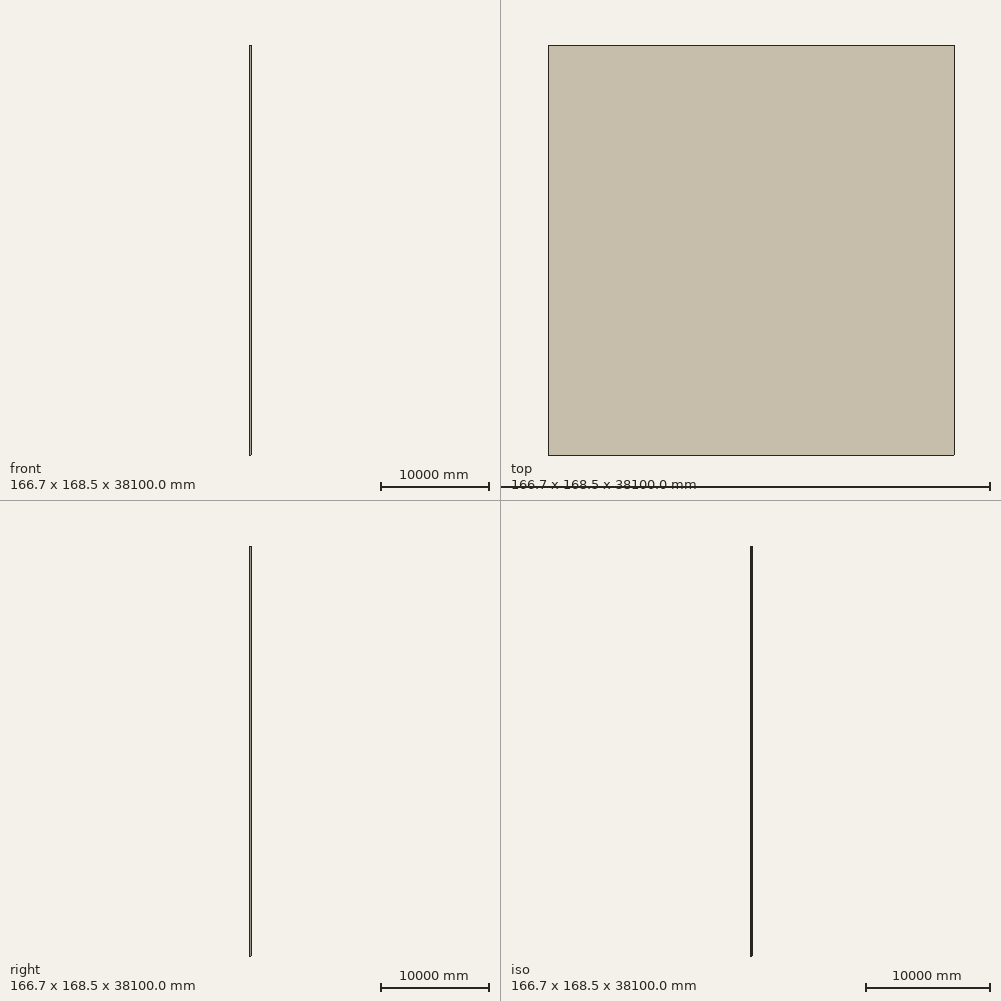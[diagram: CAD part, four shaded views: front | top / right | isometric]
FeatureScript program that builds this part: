
annotation { "Feature Type Name" : "Feature", "Feature Type Description" : "" }
export const myFeature = defineFeature(function(context is Context, id is Id, definition is map)
    precondition{}
    {
        {
            var Q0;
            Q0=qCreatedBy(makeId("Top.planeOp"),FACE);
            var sketch = newSketch(context, id + "F0", { "sketchPlane" : qUnion([Q0])});
            skLineSegment(sketch, "E0.bottom", {"start": v(-70.95, 72.43) * mm, "end": v(95.71, 72.43) * mm});
            skLineSegment(sketch, "E0.top", {"start": v(-70.95, -96.08) * mm, "end": v(95.71, -96.08) * mm});
            skLineSegment(sketch, "E0.left", {"start": v(-70.95, 72.43) * mm, "end": v(-70.95, -96.08) * mm});
            skLineSegment(sketch, "E0.right", {"start": v(95.71, 72.43) * mm, "end": v(95.71, -96.08) * mm});
            skSolve(sketch);
        }
        {
            var Q0;
            Q0=makeQuery(id+"F0.imprint","IMPRINT",FACE,{"disambiguationData":[TD([[makeQuery(id+"F0.imprint","IMPRINT",EDGE,{"derivedFrom":sQuery(id+"F0.wireOp",EDGE,"E0.bottom")}),-1.0]])]});
            extrude(context, id + "F1", {"entities" : qUnion([Q0]), "depth" : 38100 * mm, "offsetDistance" : 25.4 * mm});
        }
    });
